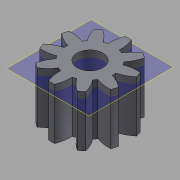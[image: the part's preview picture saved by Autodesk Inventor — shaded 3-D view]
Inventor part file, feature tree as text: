
AUTODESK INVENTOR PART (.ipt)
format: ipt  version: 2015 (Build 190159000, 159)  size: 168,448 bytes
history: native  units: in
note: dims shown in document units (in); Inventor stores cm internally (conversion verified against a paired STEP export)
features: other x13, sketch x3, plane x2
ambient origin geometry x8: Origin, YZ Plane, XZ Plane, XY Plane, X Axis, Y Axis, Z Axis, Center Point
bodies: Solid1 (feature_tree)
feature tree (18):
  other  "Spur Gear1"
  other  "Solid1::Spur Gear1"
  other  "TaggingFeature1"
  sketch  "Sketch1"  dims[d0=0.3937in]
  sketch  "Sketch2"  dims[d16=0.4528in d17=0.0in d41=0.0in d43=0.4528in d46=0.4528in d47=0.0in d48=0.0in]
  sketch  "Sketch3"
  plane  "XZ Plane_1"
  plane  "Work Plane2"
  other  "Z Axis_1"
  other  "Srf1"
  other  "Srf1::Derived"
  other  "Distance iMate"
  other  "Align iMate"
  other  "Mesh iMate"
  other  "Axis iMate"
  other  "Position iMate"
  other  "Mesh iMate2"
  other  "Start plane iMate"
